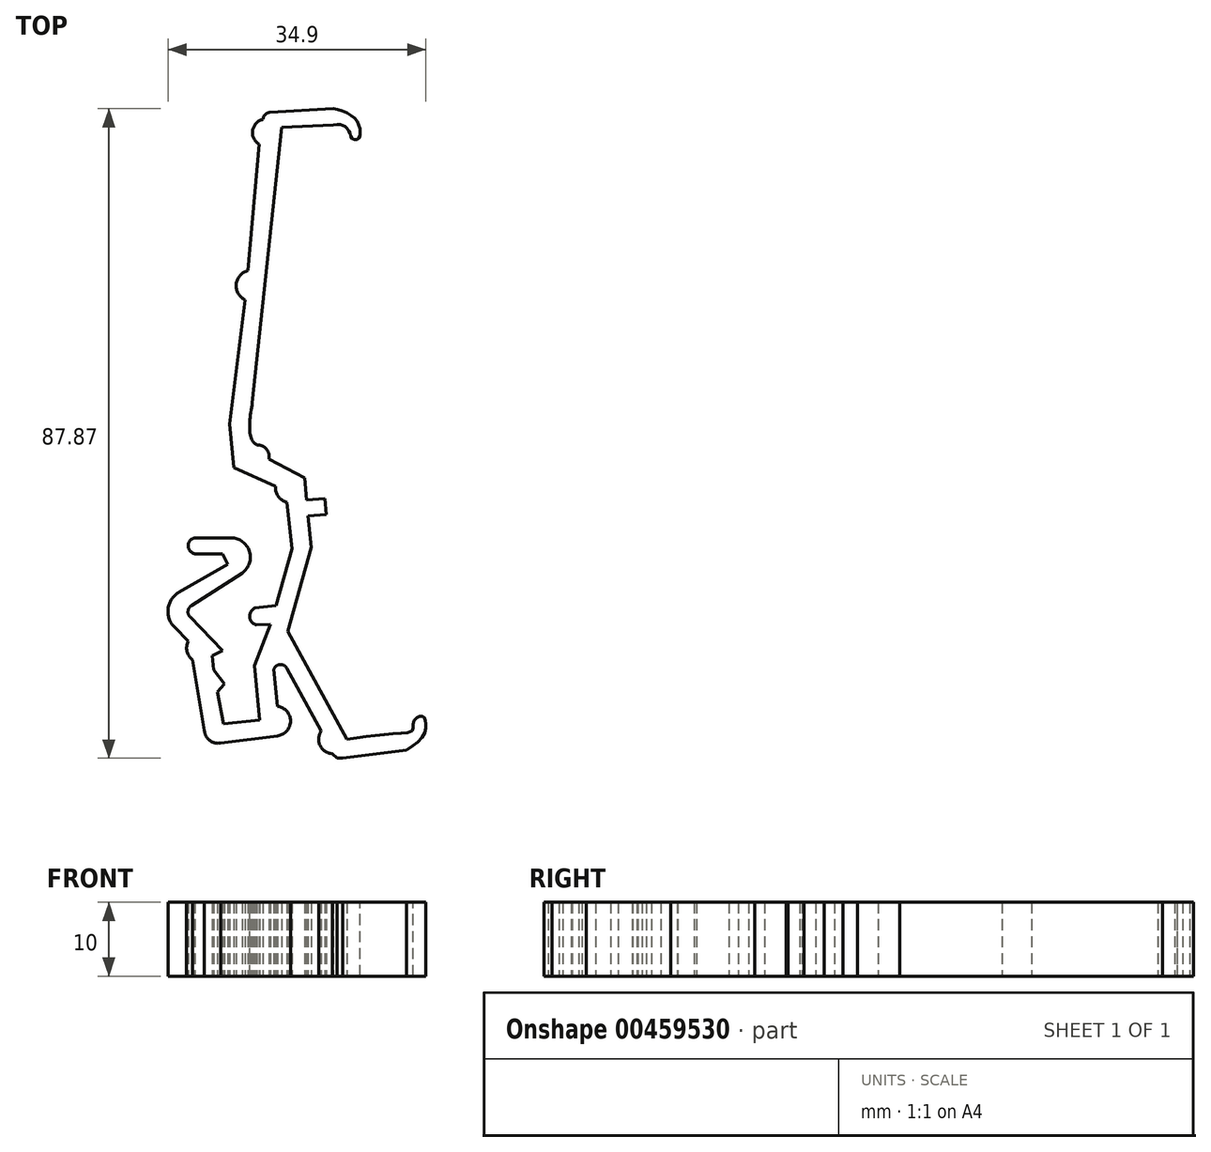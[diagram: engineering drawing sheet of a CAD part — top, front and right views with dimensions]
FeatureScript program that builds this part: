
annotation { "Feature Type Name" : "Feature", "Feature Type Description" : "" }
export const myFeature = defineFeature(function(context is Context, id is Id, definition is map)
    precondition{}
    {
        {
            var Q0;
            Q0=qCreatedBy(makeId("Top.planeOp"),FACE);
            var sketch = newSketch(context, id + "F0", { "sketchPlane" : qUnion([Q0])});
            skLineSegment(sketch, "E0", {"start": v(6.5, 10.58) * mm, "end": v(21.45, 9.31) * mm, "construction": true});
            skLineSegment(sketch, "E1", {"start": v(-47.32, 2.08) * mm, "end": v(-43.58, 2.08) * mm});
            skLineSegment(sketch, "E2", {"start": v(-43.58, 2.08) * mm, "end": v(-42.86, 0.68) * mm});
            skLineSegment(sketch, "E3", {"start": v(-42.86, 0.68) * mm, "end": v(-49.44, -3.1) * mm});
            skLineSegment(sketch, "E4", {"start": v(-47.79, -4.95) * mm, "end": v(-40.92, -0.53) * mm});
            skLineSegment(sketch, "E5", {"start": v(-47.13, 4.24) * mm, "end": v(-42.43, 4.24) * mm});
            skLineSegment(sketch, "E6", {"start": v(-50.07, -7.87) * mm, "end": v(-48.2, -9.74) * mm});
            skArc(sketch, "E7", {"start": v(-49.44, -3.1) * mm, "mid": v(-50.93, -5.34) * mm, "end": v(-50.07, -7.87) * mm});
            skArc(sketch, "E8", {"start": v(-48.2, -9.74) * mm, "mid": v(-48.38, -11.12) * mm, "end": v(-47.6, -12.28) * mm});
            skLineSegment(sketch, "E9", {"start": v(-47.6, -12.28) * mm, "end": v(-46.03, -21.8) * mm});
            skArc(sketch, "E10", {"start": v(-46.03, -21.8) * mm, "mid": v(-45.32, -23.17) * mm, "end": v(-43.82, -23.53) * mm});
            skLineSegment(sketch, "E11", {"start": v(-43.82, -23.53) * mm, "end": v(-36.14, -22.56) * mm});
            skLineSegment(sketch, "E12", {"start": v(-44.25, -16.58) * mm, "end": v(-43.41, -20.93) * mm});
            skLineSegment(sketch, "E13", {"start": v(-43.43, -20.91) * mm, "end": v(-38.52, -20.43) * mm});
            skLineSegment(sketch, "E14", {"start": v(-38.52, -20.43) * mm, "end": v(-39.24, -13.04) * mm});
            skLineSegment(sketch, "E15", {"start": v(-39.24, -13.04) * mm, "end": v(-37.08, -7.47) * mm});
            skLineSegment(sketch, "E16", {"start": v(-37.08, -7.47) * mm, "end": v(-38.99, -7.56) * mm});
            skLineSegment(sketch, "E17", {"start": v(-43.54, -11.04) * mm, "end": v(-47.96, -6.48) * mm});
            skPoint(sketch, "E18.visualSharp", {"position": v(-48.81, -5.6) * mm});
            skArc(sketch, "E18.filletArc", {"start": v(-47.79, -4.95) * mm, "mid": v(-48.24, -5.67) * mm, "end": v(-47.96, -6.48) * mm});
            skLineSegment(sketch, "E19", {"start": v(-43.54, -11.04) * mm, "end": v(-44.98, -11.71) * mm});
            skLineSegment(sketch, "E20", {"start": v(-44.98, -11.71) * mm, "end": v(-44.78, -13.62) * mm});
            skLineSegment(sketch, "E21", {"start": v(-44.78, -13.62) * mm, "end": v(-43.29, -15.52) * mm});
            skLineSegment(sketch, "E22", {"start": v(-43.29, -15.52) * mm, "end": v(-44.25, -16.58) * mm});
            skArc(sketch, "E23", {"start": v(-47.13, 4.24) * mm, "mid": v(-48.22, 3.25) * mm, "end": v(-47.32, 2.08) * mm});
            skArc(sketch, "E24", {"start": v(-40.92, -0.53) * mm, "mid": v(-39.93, 2.4) * mm, "end": v(-42.43, 4.24) * mm});
            skLineSegment(sketch, "E25", {"start": v(-36.13, -18.57) * mm, "end": v(-36.62, -13.57) * mm});
            skLineSegment(sketch, "E26", {"start": v(-34.85, -13.41) * mm, "end": v(-30.2, -21.9) * mm});
            skArc(sketch, "E27", {"start": v(-34.85, -13.41) * mm, "mid": v(-35.79, -12.91) * mm, "end": v(-36.62, -13.57) * mm});
            skArc(sketch, "E28", {"start": v(-30.2, -21.9) * mm, "mid": v(-30.42, -23.77) * mm, "end": v(-28.97, -24.95) * mm});
            skLineSegment(sketch, "E29", {"start": v(-27.3, -25.57) * mm, "end": v(-18.67, -24.5) * mm});
            skArc(sketch, "E30", {"start": v(-36.14, -22.56) * mm, "mid": v(-34.38, -20.57) * mm, "end": v(-36.13, -18.57) * mm});
            skArc(sketch, "E31", {"start": v(-39.2, -5.27) * mm, "mid": v(-39.9, -6.49) * mm, "end": v(-38.99, -7.56) * mm});
            skLineSegment(sketch, "E32", {"start": v(-39.2, -5.27) * mm, "end": v(-36.32, -4.94) * mm});
            skLineSegment(sketch, "E33", {"start": v(-36.32, -4.94) * mm, "end": v(-34.19, 2.78) * mm});
            skLineSegment(sketch, "E34", {"start": v(-34.19, 2.78) * mm, "end": v(-34.85, 9.04) * mm});
            skLineSegment(sketch, "E35", {"start": v(-36.39, 11.17) * mm, "end": v(-42.04, 13.75) * mm});
            skArc(sketch, "E36", {"start": v(-36.39, 11.17) * mm, "mid": v(-36.02, 9.82) * mm, "end": v(-34.85, 9.04) * mm});
            skLineSegment(sketch, "E37", {"start": v(-42.04, 13.75) * mm, "end": v(-42.6, 19.62) * mm});
            skLineSegment(sketch, "E38", {"start": v(-42.6, 19.62) * mm, "end": v(-40.51, 36.42) * mm});
            skArc(sketch, "E39", {"start": v(-40.1, 40.4) * mm, "mid": v(-41.72, 38.56) * mm, "end": v(-40.51, 36.42) * mm});
            skLineSegment(sketch, "E40", {"start": v(-40.1, 40.4) * mm, "end": v(-38.6, 57.49) * mm});
            skArc(sketch, "E41", {"start": v(-38.1, 60.85) * mm, "mid": v(-39.5, 59.34) * mm, "end": v(-38.6, 57.49) * mm});
            skArc(sketch, "E42", {"start": v(-37.17, 61.8) * mm, "mid": v(-37.8, 61.5) * mm, "end": v(-38.1, 60.85) * mm});
            skLineSegment(sketch, "E43", {"start": v(-37.17, 61.8) * mm, "end": v(-28.6, 62.3) * mm});
            skFitSpline(sketch, "E44", {"points": [v(-28.6, 62.3) * mm, v(-27.41, 62.04) * mm, v(-26.13, 61.37) * mm, v(-25.44, 60.73) * mm, v(-25.03, 59.82) * mm, v(-24.94, 59.04) * mm, v(-25.03, 58.47) * mm, v(-25.24, 58.2) * mm, v(-25.45, 58.13) * mm, v(-25.87, 58.19) * mm, v(-26.13, 58.33) * mm, v(-26.27, 58.78) * mm, v(-26.44, 59.22) * mm, v(-26.75, 59.7) * mm, v(-27.06, 59.96) * mm, v(-27.48, 60.1) * mm, v(-27.8, 60.16) * mm, v(-28.6, 60.11) * mm], "startDerivative": vector(14.17, -2.05) * mm, "endDerivative": vector(-7.35, -0.18) * mm});
            skLineSegment(sketch, "E45", {"start": v(-28.6, 60.11) * mm, "end": v(-35.6, 59.78) * mm});
            skLineSegment(sketch, "E46", {"start": v(-35.6, 59.78) * mm, "end": v(-39.54, 22.53) * mm});
            skFitSpline(sketch, "E47", {"points": [v(-39.54, 22.53) * mm, v(-39.91, 19.26) * mm, v(-39.54, 17.4) * mm, v(-38.95, 16.81) * mm], "startDerivative": vector(-1.3, -7.7) * mm, "endDerivative": vector(2.87, -2.1) * mm});
            skArc(sketch, "E48", {"start": v(-37.32, 14.78) * mm, "mid": v(-37.61, 16.22) * mm, "end": v(-38.95, 16.81) * mm});
            skLineSegment(sketch, "E49", {"start": v(-37.35, 14.9) * mm, "end": v(-32.29, 12.23) * mm});
            skLineSegment(sketch, "E50", {"start": v(-32.48, 12.33) * mm, "end": v(-32.2, 9.35) * mm});
            skLineSegment(sketch, "E51", {"start": v(-31.6, 2.94) * mm, "end": v(-34.73, -8.44) * mm});
            skLineSegment(sketch, "E52", {"start": v(-29.75, 9.58) * mm, "end": v(-29.55, 7.42) * mm});
            skLineSegment(sketch, "E53", {"start": v(-29.75, 9.58) * mm, "end": v(-32.2, 9.35) * mm});
            skLineSegment(sketch, "E54", {"start": v(-29.55, 7.42) * mm, "end": v(-32, 7.19) * mm});
            skLineSegment(sketch, "E55.trimOffspring", {"start": v(-32, 7.19) * mm, "end": v(-31.6, 2.94) * mm});
            skLineSegment(sketch, "E56", {"start": v(-26.7, -23.02) * mm, "end": v(-34.73, -8.44) * mm});
            skFitSpline(sketch, "E57", {"points": [v(-26.7, -23.02) * mm, v(-20.5, -22.3) * mm, v(-17.83, -21.77) * mm, v(-17.78, -20.83) * mm, v(-17.2, -20.06) * mm, v(-16.58, -19.88) * mm, v(-16.19, -20.24) * mm, v(-16.06, -20.89) * mm, v(-16.36, -22.46) * mm, v(-18.67, -24.5) * mm], "startDerivative": vector(29.59, 4.12) * mm, "endDerivative": vector(-18.66, -12.55) * mm});
            skLineSegment(sketch, "E58", {"start": v(-28.97, -24.95) * mm, "end": v(-28.72, -24.99) * mm});
            skLineSegment(sketch, "E59", {"start": v(-28.72, -24.99) * mm, "end": v(-28.1, -25.57) * mm});
            skLineSegment(sketch, "E60", {"start": v(-28.1, -25.57) * mm, "end": v(-27.3, -25.57) * mm});
            skSolve(sketch);
        }
        {
            var Q0;
            Q0 = qSketchRegion(id + "F0", true);
            extrude(context, id + "F1", {"entities" : qUnion([Q0]), "depth" : 10 * mm});
        }
    });
